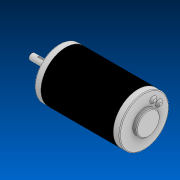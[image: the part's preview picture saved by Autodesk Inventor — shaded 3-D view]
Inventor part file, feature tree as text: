
AUTODESK INVENTOR PART (.ipt)
format: ipt  version: 2022.2 (Build 262287000, 287)  size: 162,816 bytes
history: native  units: in
note: dims shown in document units (in); Inventor stores cm internally (conversion verified against a paired STEP export)
features: chamfer x1
ambient origin geometry x8: Origin, YZ Plane, XZ Plane, XY Plane, X Axis, Y Axis, Z Axis, Center Point
bodies: Solid1 (feature_tree)
feature tree (1):
  chamfer  "Chamfer3"  [1 undecoded]
note: 1 required parameter value undecoded (feature->parameter linkage not recoverable at this tier; creation-order binding heuristic only, values carry confidence <= 0.55)
